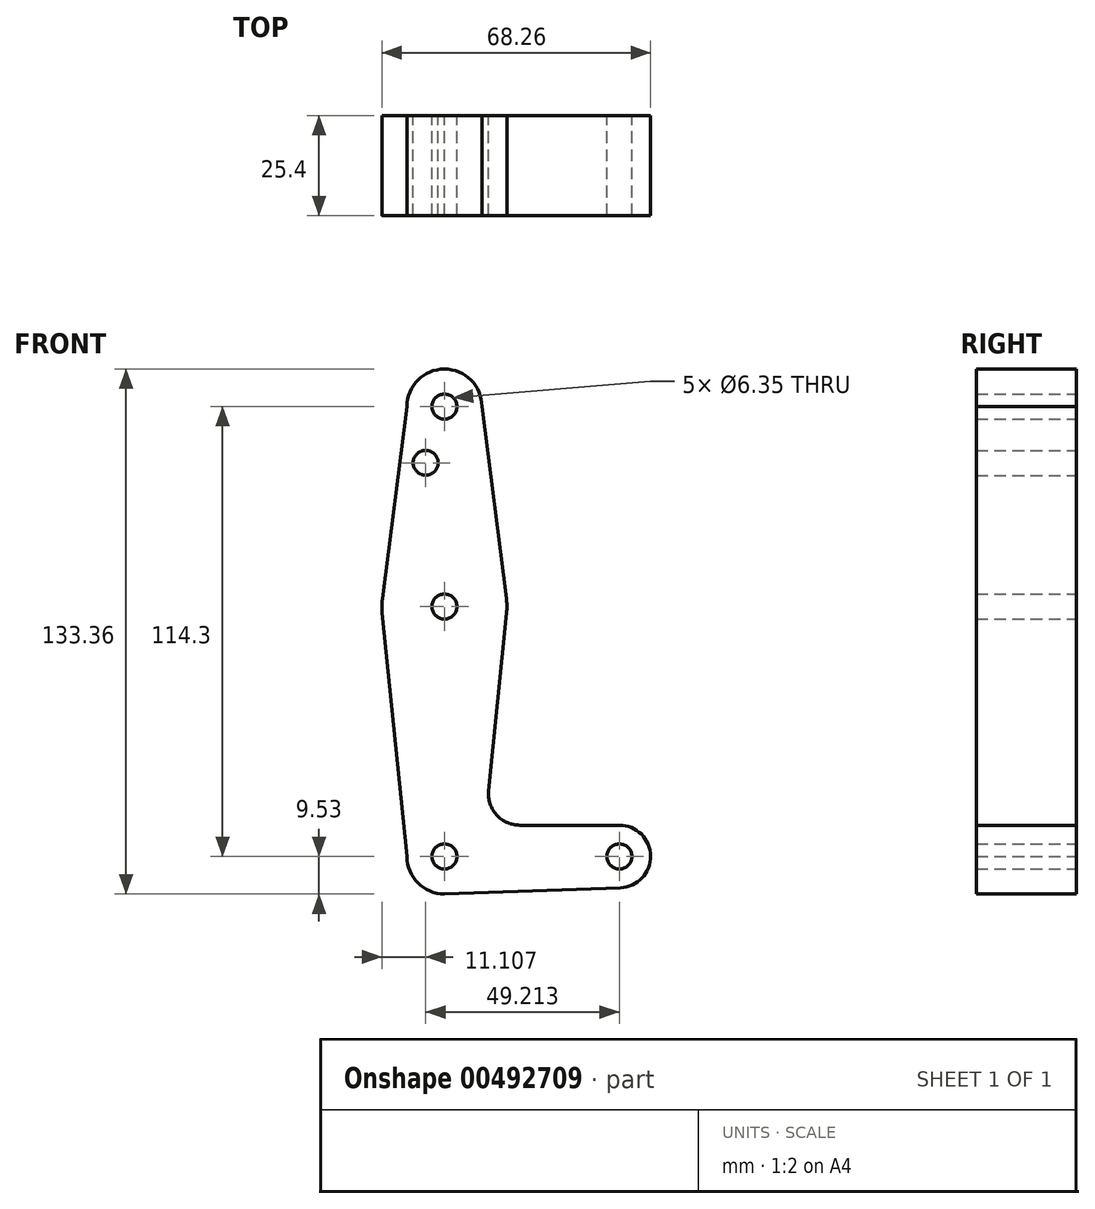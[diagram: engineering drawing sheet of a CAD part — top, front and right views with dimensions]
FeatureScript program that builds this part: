
annotation { "Feature Type Name" : "Feature", "Feature Type Description" : "" }
export const myFeature = defineFeature(function(context is Context, id is Id, definition is map)
    precondition{}
    {
        {
            var Q0;
            Q0=qCreatedBy(makeId("Front.planeOp"),FACE);
            var sketch = newSketch(context, id + "F0", { "sketchPlane" : qUnion([Q0])});
            skLineSegment(sketch, "E0", {"start": v(0, 0) * mm, "end": v(0, 114.3) * mm, "construction": true});
            skCircle(sketch, "E1", {"center": v(0, 0) * mm, "radius": 9.53 * mm});
            skCircle(sketch, "E2", {"center": v(0, 63.5) * mm, "radius": 15.88 * mm});
            skCircle(sketch, "E3", {"center": v(0, 114.3) * mm, "radius": 9.53 * mm});
            skCircle(sketch, "E4", {"center": v(44.45, 0) * mm, "radius": 7.94 * mm});
            skLineSegment(sketch, "E5", {"start": v(0, 0) * mm, "end": v(44.45, 0) * mm, "construction": true});
            skLineSegment(sketch, "E6", {"start": v(9.53, 114.3) * mm, "end": v(15.75, 65.5) * mm});
            skLineSegment(sketch, "E7", {"start": v(-9.52, 114.3) * mm, "end": v(-15.75, 65.5) * mm});
            skLineSegment(sketch, "E8", {"start": v(19.16, 7.94) * mm, "end": v(44.45, 7.94) * mm});
            skLineSegment(sketch, "E9", {"start": v(0, -9.53) * mm, "end": v(44.73, -7.93) * mm});
            skLineSegment(sketch, "E10", {"start": v(11.25, 16.68) * mm, "end": v(15.8, 61.91) * mm});
            skLineSegment(sketch, "E11", {"start": v(-9.52, 0) * mm, "end": v(-15.8, 61.91) * mm});
            skCircle(sketch, "E12", {"center": v(0, 63.5) * mm, "radius": 3.18 * mm});
            skCircle(sketch, "E13", {"center": v(-4.76, 100.03) * mm, "radius": 3.18 * mm});
            skCircle(sketch, "E14", {"center": v(0, 114.3) * mm, "radius": 3.18 * mm});
            skCircle(sketch, "E15", {"center": v(0, 0) * mm, "radius": 3.18 * mm});
            skCircle(sketch, "E16", {"center": v(44.45, 0) * mm, "radius": 3.18 * mm});
            skArc(sketch, "E17.filletArc", {"start": v(11.25, 16.68) * mm, "mid": v(13.26, 10.55) * mm, "end": v(19.16, 7.94) * mm});
            skSolve(sketch);
        }
        {
            var Q0;
            Q0=makeQuery(id+"F0.imprint","IMPRINT",FACE,{"disambiguationData":[TD([[makeQuery(id+"F0.imprint","IMPRINT",EDGE,{"derivedFrom":sQuery(id+"F0.wireOp",EDGE,"E14")}),-1.0]])]});
            var Q1;
            {var subQ1=sQuery(id+"F0.wireOp",EDGE,"E6");Q1=makeQuery(id+"F0.imprint","IMPRINT",FACE,{"disambiguationData":[TD([[makeQuery(id+"F0.imprint","IMPRINT",EDGE,{"derivedFrom":subQ1}),-1.0]])]});}
            var Q2;
            Q2=makeQuery(id+"F0.imprint","IMPRINT",FACE,{"disambiguationData":[TD([[makeQuery(id+"F0.imprint","IMPRINT",EDGE,{"derivedFrom":sQuery(id+"F0.wireOp",EDGE,"E12")}),-1.0]])]});
            var Q3;
            {var subQ0=sQuery(id+"F0.wireOp",EDGE,"E8");Q3=makeQuery(id+"F0.imprint","IMPRINT",FACE,{"disambiguationData":[TD([[makeQuery(id+"F0.imprint","IMPRINT",EDGE,{"derivedFrom":subQ0}),-1.0]])]});}
            var Q4;
            Q4=makeQuery(id+"F0.imprint","IMPRINT",FACE,{"disambiguationData":[TD([[makeQuery(id+"F0.imprint","IMPRINT",EDGE,{"derivedFrom":sQuery(id+"F0.wireOp",EDGE,"E15")}),-1.0]])]});
            var Q5;
            Q5=makeQuery(id+"F0.imprint","IMPRINT",FACE,{"disambiguationData":[TD([[makeQuery(id+"F0.imprint","IMPRINT",EDGE,{"derivedFrom":sQuery(id+"F0.wireOp",EDGE,"E16")}),-1.0]])]});
            extrude(context, id + "F1", {"entities" : qUnion([Q0, Q1, Q2, Q3, Q4, Q5]), "depth" : 25.4 * mm, "offsetDistance" : 25.4 * mm});
        }
    });
